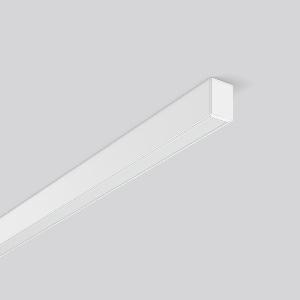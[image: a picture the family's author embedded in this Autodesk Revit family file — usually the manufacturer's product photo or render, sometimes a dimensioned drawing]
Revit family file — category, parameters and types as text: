
# Revit family: less_is_more_27_312199_002_3155
name_source: partatom
category: Lighting Fixtures
units: mm (PartAtom-declared; Revit-internal decimal feet)

## family parameters
Cut with Voids When Loaded = No
Host = Face
Light Source = No
Part Type = Normal
Room Calculation Point = No
Round Connector Dimension = Use Diameter
Shared = No

## types (1)
- LESS IS MORE 27 (1 x LED Modul 830, 2600 lm, 3000)
    Apparent Load = 34 VA
    CIE Flux Codes = 65 89 98 100 100
    Color Rendering = 80
    Color Temperature = 3000
    Default Elevation = 1800 mm
    Description = Series: LESS IS MORE 27
Ceiling luminaire with slim design. Housing: extruded aluminium profile, powder-coated. End cap aluminium powder-coated. Diffuser made of non-yellowing plastic (PMMA) microprismatic. Suitable for Ceiling mounting, Wall (surface). External driver with connecting cable. 
Colour: traffic white, matt (RAL 9016)
Length: 1212 mm
Width: 28 mm
Height: 38 mm
Lamp: LED
Socket: without socket
Colour temperature: 3000K
Colour rendering index (CRI): 82
System power: 34 W
Rated luminous flux: 2600 lm
Luminous efficiency: 76 lm/W
Control gear: Regulated power supply
Protection class: II
Type of protection: IP 20
    Height = 38 mm
    Lamp = 1 x LED Modul 830
    Lamp Light Flux = 2600 lm
    Lamp count = 1
    Length = 1212 mm
    Lifetime = 50000 h
    Luminous efficacy = 76 lm/W
    Manufacturer = RZB
    ModVariant = No
    Model = 312199.002
    Mounting Place = Ceiling, Wall
    Mounting Type = Surface mounted
    Number of Poles = 1
    OnlyDefault = Yes
    Power Factor = 1
    Product Name = LESS IS MORE 27
    Product group = Surface mounted LED linear luminaires
    ProductGroupID = 307
    Protection Class = Protection class II
    Protection Degree = IP 20
    RLX_Detail_Level = 1
    RLX_Emergency_Light_Flux = 0 lm
    RLX_Emergency_Type = 0
    RLX_Emergency_Type_DB = No
    RlxData = <blob elided: 24733 chars, md5=3b439488>
    Socket = socket
    Standby Power = 0 W
    System Light Flux = 2600 lm
    System Power = 34 W
    Type Comments = Product without accessories
    Type Image = 312197.002.jpg
    URL = http://relux.com
    VarID = ---
    Voltage = 230 V
    Voltage Range = 220-240 V
    Weight = 0.00 kg
    Width = 28 mm

## geometry (parser evidence)
native form markers: Blend x4, Sweep x12
no freeform markers — native parametric forms only
